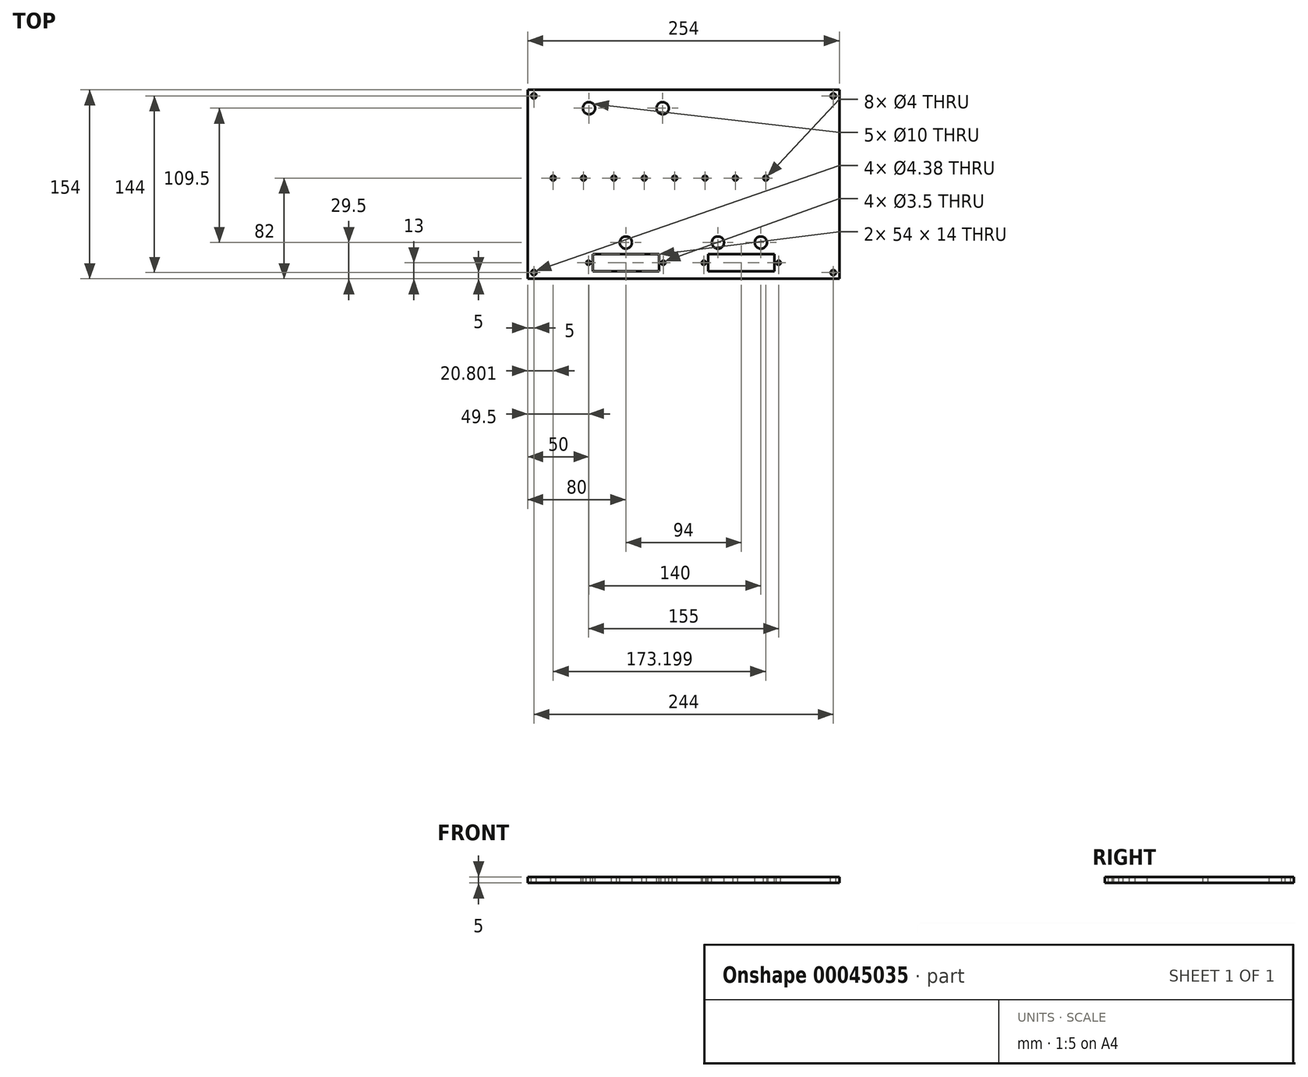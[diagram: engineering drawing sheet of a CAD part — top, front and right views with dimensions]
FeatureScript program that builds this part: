
annotation { "Feature Type Name" : "Feature", "Feature Type Description" : "" }
export const myFeature = defineFeature(function(context is Context, id is Id, definition is map)
    precondition{}
    {
        {
            var Q0;
            Q0=qCreatedBy(makeId("Top.planeOp"),FACE);
            var sketch = newSketch(context, id + "F0", { "sketchPlane" : qUnion([Q0])});
            skLineSegment(sketch, "E0.rect.bottom", {"start": v(-127, 77) * mm, "end": v(127, 77) * mm});
            skLineSegment(sketch, "E0.rect.top", {"start": v(-127, -77) * mm, "end": v(127, -77) * mm});
            skLineSegment(sketch, "E0.rect.left", {"start": v(-127, 77) * mm, "end": v(-127, -77) * mm});
            skLineSegment(sketch, "E0.rect.right", {"start": v(127, 77) * mm, "end": v(127, -77) * mm});
            skPoint(sketch, "E0.rect.middle", {"position": v(0, 0) * mm});
            skSolve(sketch);
        }
        {
            var Q0;
            Q0 = qSketchRegion(id + "F0", true);
            extrude(context, id + "F1", {"entities" : qUnion([Q0]), "depth" : 5 * mm});
        }
        {
            var Q0;
            Q0=makeQuery(id+"F1.opExtrude","CAP_FACE",FACE,{"disambiguationData":[OSD([sQuery(id+"F0.wireOp",EDGE,"E0.rect.bottom"),sQuery(id+"F0.wireOp",EDGE,"E0.rect.top"),sQuery(id+"F0.wireOp",EDGE,"E0.rect.left"),sQuery(id+"F0.wireOp",EDGE,"E0.rect.right")])],"isStart":false});
            var sketch = newSketch(context, id + "F2", { "sketchPlane" : qUnion([Q0])});
            skCircle(sketch, "E1", {"center": v(-122, 72) * mm, "radius": 2.19 * mm});
            skLineSegment(sketch, "E2", {"start": v(0, 0) * mm, "end": v(0, 77) * mm, "construction": true});
            skLineSegment(sketch, "E3", {"start": v(0, 0) * mm, "end": v(-127, 0) * mm, "construction": true});
            skCircle(sketch, "E4.MirrorC", {"center": v(122, 72) * mm, "radius": 2.19 * mm});
            skCircle(sketch, "E5.MirrorC", {"center": v(-122, -72) * mm, "radius": 2.19 * mm});
            skCircle(sketch, "E6.MirrorC", {"center": v(122, -72) * mm, "radius": 2.19 * mm});
            skLineSegment(sketch, "E7", {"start": v(-127, 5) * mm, "end": v(127, 5) * mm, "construction": true});
            skCircle(sketch, "E8", {"center": v(-77, 62) * mm, "radius": 5 * mm});
            skCircle(sketch, "E9.1.0.0", {"center": v(-17, 62) * mm, "radius": 5 * mm});
            skLineSegment(sketch, "E9.direction1", {"start": v(-77, 62) * mm, "end": v(-17, 62) * mm, "construction": true});
            skCircle(sketch, "E10", {"center": v(-47, -47.5) * mm, "radius": 5 * mm});
            skCircle(sketch, "E11", {"center": v(28, -47.5) * mm, "radius": 5 * mm});
            skCircle(sketch, "E12", {"center": v(63, -47.5) * mm, "radius": 5 * mm});
            skLineSegment(sketch, "E13.rect.bottom", {"start": v(-74, -57) * mm, "end": v(-20, -57) * mm});
            skLineSegment(sketch, "E13.rect.top", {"start": v(-74, -71) * mm, "end": v(-20, -71) * mm});
            skLineSegment(sketch, "E13.rect.left", {"start": v(-74, -57) * mm, "end": v(-74, -71) * mm});
            skLineSegment(sketch, "E13.rect.right", {"start": v(-20, -57) * mm, "end": v(-20, -71) * mm});
            skPoint(sketch, "E13.rect.middle", {"position": v(-47, -64) * mm});
            skCircle(sketch, "E14", {"center": v(-77.5, -64) * mm, "radius": 1.75 * mm});
            skCircle(sketch, "E15", {"center": v(67, 5) * mm, "radius": 2 * mm});
            skCircle(sketch, "E16.1.0.0", {"center": v(42.26, 5) * mm, "radius": 2 * mm});
            skCircle(sketch, "E16.2.0.0", {"center": v(17.51, 5) * mm, "radius": 2 * mm});
            skCircle(sketch, "E16.3.0.0", {"center": v(-7.23, 5) * mm, "radius": 2 * mm});
            skCircle(sketch, "E16.4.0.0", {"center": v(-31.97, 5) * mm, "radius": 2 * mm});
            skCircle(sketch, "E16.5.0.0", {"center": v(-56.71, 5) * mm, "radius": 2 * mm});
            skCircle(sketch, "E16.6.0.0", {"center": v(-81.46, 5) * mm, "radius": 2 * mm});
            skCircle(sketch, "E16.7.0.0", {"center": v(-106.2, 5) * mm, "radius": 2 * mm});
            skLineSegment(sketch, "E16.direction1", {"start": v(67, 5) * mm, "end": v(42.26, 5) * mm, "construction": true});
            skLineSegment(sketch, "E17", {"start": v(-47, -64) * mm, "end": v(-47, -47.5) * mm, "construction": true});
            skCircle(sketch, "E18.MirrorC", {"center": v(-16.5, -64) * mm, "radius": 1.75 * mm});
            skCircle(sketch, "E19.MirrorC", {"center": v(16.5, -64) * mm, "radius": 1.75 * mm});
            skCircle(sketch, "E20.MirrorC", {"center": v(77.5, -64) * mm, "radius": 1.75 * mm});
            skLineSegment(sketch, "E21.MirrorCS", {"start": v(20, -57) * mm, "end": v(20, -71) * mm});
            skLineSegment(sketch, "E22.MirrorCS", {"start": v(74, -71) * mm, "end": v(20, -71) * mm});
            skLineSegment(sketch, "E23.MirrorCS", {"start": v(74, -57) * mm, "end": v(74, -71) * mm});
            skLineSegment(sketch, "E24.MirrorCS", {"start": v(74, -57) * mm, "end": v(20, -57) * mm});
            skSolve(sketch);
        }
        {
            var Q0;
            Q0 = qSketchRegion(id + "F2", true);
            extrude(context, id + "F3", {"entities" : qUnion([Q0]), "operationType" : NewBodyOperationType.REMOVE, "endBound" : BoundingType.THROUGH_ALL, "oppositeDirection" : true, "depth" : 25 * mm});
        }
    });
